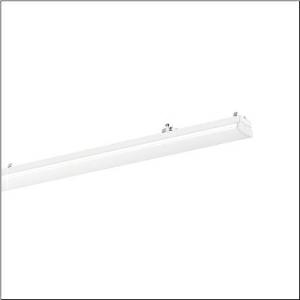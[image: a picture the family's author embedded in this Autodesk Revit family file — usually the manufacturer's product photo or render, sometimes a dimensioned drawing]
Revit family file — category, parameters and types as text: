
# Revit family: licross_21_recessed_opal_mo_52tl1dmn4axg
name_source: partatom
category: Lighting Fixtures
units: mm (PartAtom-declared; Revit-internal decimal feet)

## family parameters
Cut with Voids When Loaded = No
Host = Face
Light Source = No
Part Type = Normal
Room Calculation Point = No
Round Connector Dimension = Use Diameter
Shared = No

## types (1)
- --- (1 x LED, 10420 lm, 60.5 W, 4000K)
    Apparent Load = 61 VA
    CIE Flux Codes = 44 73 91 87 100
    Color Rendering = 80
    Color Temperature = 4000K
    Default Elevation = 1800 mm
    Description = Licross 21 recessed opal MO, luminaire insert, of sheet steel, galvanised, coil coated, white, length: 1.500mm, width: 66mm, height: 67mm, LED rated luminous flux: 10.420lm, light colour: 840, SDCM (Standard Deviation of Colour Matching)MacAdam ≤ 3 SDCM (initial), control gear: ON/OFF Multilumen, with plug, 3-pole, with phase selection, mains connection: 220..240V, AC, 50/60Hz, rated input power: 61W, internal wiring halogen-free, primary optical cover: cover, of PMMA, light emission: direct with ceiling illumination distribution, primary light characteristic: symmetric, protection rating (complete): IP40, insulation class (complete): insulation class I (protective earthing), certification: CE, ENEC, VDE, UKCA, protection symbol: D if used in an environment without relevant dust loads with corresponding accessories, impact resistance: IK06, permissible ambient temperature for indoor applications: -35..+40°C, corresponds to IFS (International Featured Standards) requirements for safety and quality in the food industry, reducing of maximum allowable ambient temperature of 5°C with ceiling mounting, LABS conformity tested according to VDMA 24364:2018-05, The light source and the operating device comply with the requirements of the Ecodesign Regulation (EU) 2019/2020 and are replaceable in accordance with this regulation, packaging unit: 1 piece
    Height = 83 mm
    Lamp = 1 x LED
    Lamp Light Flux = 10420 lm
    Lamp Power = 60.5 W
    Lamp count = 1
    Length = 1500 mm
    Luminous efficacy = 172 lm/W
    Manufacturer = Siteco
    ModVariant = No
    Model = 52TL1DMN4AXG
    Mounting Place = Ceiling
    Mounting Type = Pendant
    Number of Poles = 1
    OnlyDefault = Yes
    Power Factor = 1
    Product Name = Licross 21 recessed opal MO
    Product group = luminaire insert | ceiling pendant
    ProductGroupID = 901
    Protection Class = Protection class I
    Protection Degree = IP 40
    RLX_Detail_Level = 1
    RLX_Emergency_Light_Flux = 0 lm
    RLX_Emergency_Type = 0
    RLX_Emergency_Type_DB = No
    RlxData = <blob elided: 24833 chars, md5=cdc216d4>
    Socket = socket
    Standby Power = 0 W
    System Light Flux = 10420 lm
    System Power = 61 W
    Type Comments = factory setting: luminous flux: 100 % | (A | C | E) | 140 mA
    Type Image = l_1313666.jpg
    URL = http://relux.com
    VarID = @adj_072347
    Voltage = 0 V
    Weight = 0.00 kg
    Width = 76 mm

## geometry (parser evidence)
native form markers: Blend x4, Sweep x13
no freeform markers — native parametric forms only
